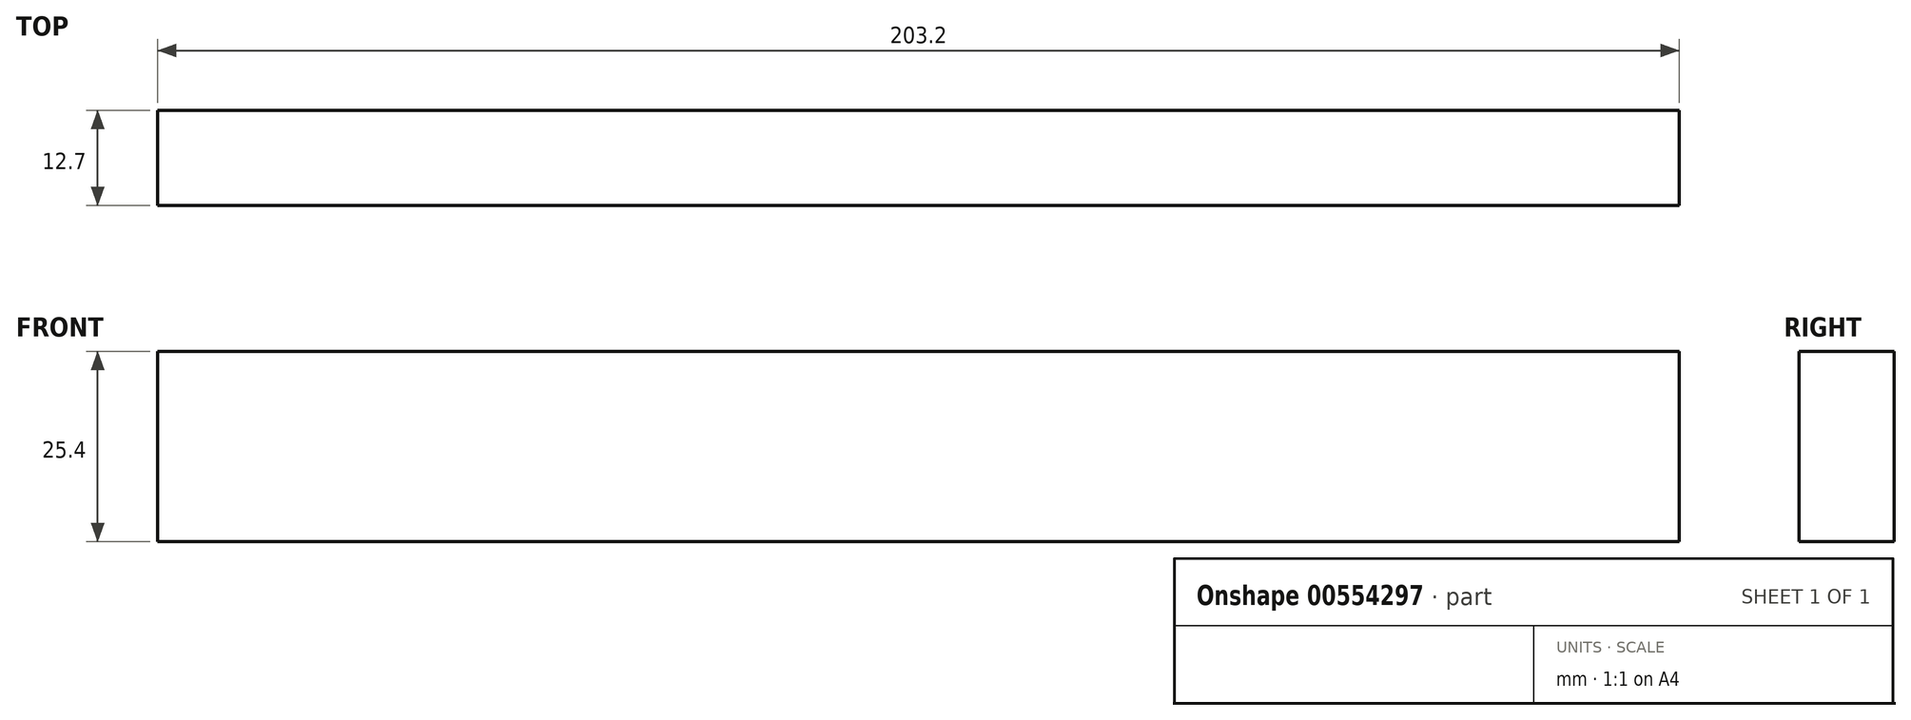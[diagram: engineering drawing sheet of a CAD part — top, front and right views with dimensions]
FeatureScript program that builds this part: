
annotation { "Feature Type Name" : "Feature", "Feature Type Description" : "" }
export const myFeature = defineFeature(function(context is Context, id is Id, definition is map)
    precondition{}
    {
        {
            var Q0;
            Q0=qCreatedBy(makeId("Front.planeOp"),FACE);
            var sketch = newSketch(context, id + "F0", { "sketchPlane" : qUnion([Q0])});
            skLineSegment(sketch, "E0.bottom", {"start": v(-79.71, 11.01) * mm, "end": v(123.49, 11.01) * mm});
            skLineSegment(sketch, "E0.top", {"start": v(-79.71, -14.39) * mm, "end": v(123.49, -14.39) * mm});
            skLineSegment(sketch, "E0.left", {"start": v(-79.71, 11.01) * mm, "end": v(-79.71, -14.39) * mm});
            skLineSegment(sketch, "E0.right", {"start": v(123.49, 11.01) * mm, "end": v(123.49, -14.39) * mm});
            skSolve(sketch);
        }
        {
            var Q0;
            Q0 = qSketchRegion(id + "F0", true);
            extrude(context, id + "F1", {"entities" : qUnion([Q0]), "depth" : 12.7 * mm, "offsetDistance" : 25.4 * mm});
        }
    });
